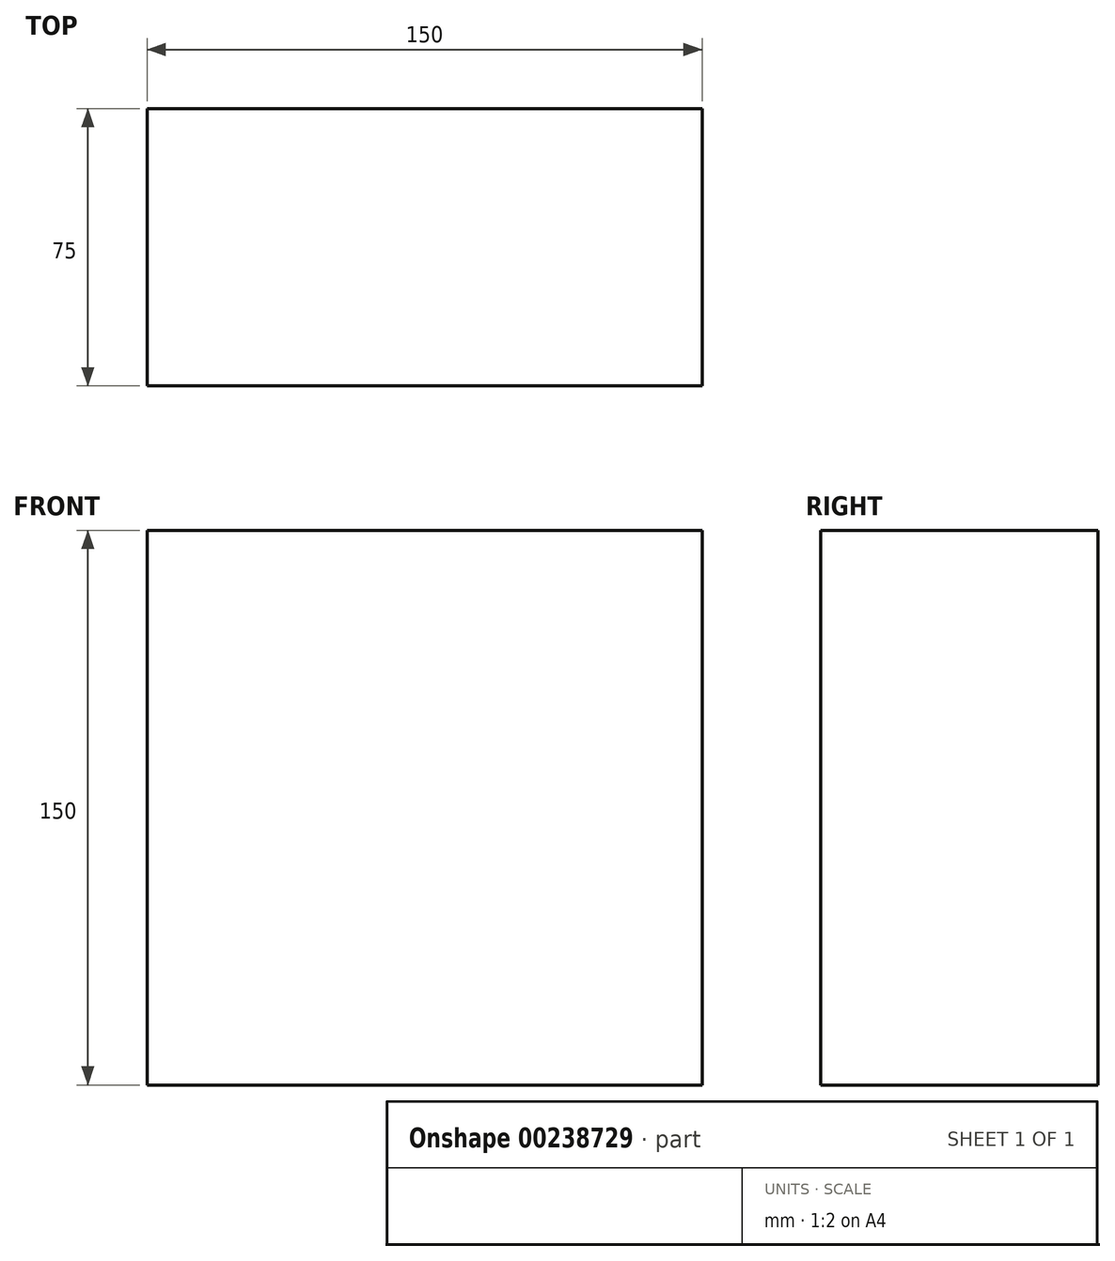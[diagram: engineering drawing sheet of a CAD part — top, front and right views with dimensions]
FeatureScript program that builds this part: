
annotation { "Feature Type Name" : "Feature", "Feature Type Description" : "" }
export const myFeature = defineFeature(function(context is Context, id is Id, definition is map)
    precondition{}
    {
        {
            var Q0;
            Q0=qCreatedBy(makeId("Top.planeOp"),FACE);
            var sketch = newSketch(context, id + "F0", { "sketchPlane" : qUnion([Q0])});
            skLineSegment(sketch, "E0.bottom", {"start": v(0, 1.5) * mm, "end": v(150, 1.5) * mm});
            skLineSegment(sketch, "E0.top", {"start": v(0, 76.5) * mm, "end": v(150, 76.5) * mm});
            skLineSegment(sketch, "E0.left", {"start": v(0, 1.5) * mm, "end": v(0, 76.5) * mm});
            skLineSegment(sketch, "E0.right", {"start": v(150, 1.5) * mm, "end": v(150, 76.5) * mm});
            skSolve(sketch);
        }
        {
            var Q0;
            Q0 = qSketchRegion(id + "F0", true);
            extrude(context, id + "F1", {"entities" : qUnion([Q0]), "depth" : 150 * mm});
        }
    });
